# Revit family: expandable light position 2
name_source: partatom
category: Lighting Fixtures
units: mm (PartAtom-declared; Revit-internal decimal feet)

## family parameters
Always vertical = Yes
Cut with Voids When Loaded = No
Light Source = Yes
Maintain Annotation Orientation = No
OmniClass Number = 23.80.70.00
OmniClass Title = Lighting
Part Type = Normal
Room Calculation Point = No
Round Connector Dimension = Use Diameter
Shared = No
Work Plane-Based = No

## types (16) — shared parameters
Color Filter = 16777215
Default Elevation = 0' - 0"
Dimming Lamp Color Temperature Shift = <None>
MATERIAL CABLE = Steel, Paint Finish, Ivory, Glossy
MATERIAL LIGHT PIECE = Cloth, Lamp Shade
MATERIAL LIGHT PIECE ATTACHMENT = Steel, Paint Finish, Ivory, Glossy
MATERIAL ROOF ATTACHMENT PIECE = Steel, Paint Finish, Ivory, Glossy
Tilt Angle = 60.00°

## per-type parameters (varying)
| type | BOTTOM LIGHT PIECE HEIGHT | FLOOR TO ROOF HEIGHT | Photometric Web File | SUSPENDED CABLE LENGTH | TOP LIGHT PIECE HEIGHT |
| Totem Up-Down A-A | 1' - 2" | 9' - 0" | STELLA （D750MM）_IESNA2002.IES | 3' - 0" | 1' - 2" |
| Totem Up-Down A-B | 1' - 2" | 0' - 1 17/32" | generic | 2' - 0" | 0' - 10" |
| Totem Up-Down A-C | 1' - 2" | 0' - 1 17/32" | generic | 2' - 0" | 0' - 4 1/4" |
| Totem Up-Down A-D | 1' - 2" | 0' - 1 17/32" | generic | 2' - 0" | 0' - 3 13/32" |
| Totem Up-Down B-A | 0' - 10" | 0' - 1 17/32" | generic | 2' - 0" | 1' - 2" |
| Totem Up-Down B-B | 0' - 10" | 0' - 1 17/32" | generic | 2' - 0" | 0' - 10" |
| Totem Up-Down B-C | 0' - 10" | 0' - 1 17/32" | generic | 2' - 0" | 0' - 4 1/4" |
| Totem Up-Down B-D | 0' - 10" | 0' - 1 17/32" | generic | 2' - 0" | 0' - 3 13/32" |
| Totem Up-Down C-A | 0' - 4 1/4" | 0' - 1 17/32" | generic | 2' - 0" | 1' - 2" |
| Totem Up-Down C-B | 0' - 4 1/4" | 0' - 1 17/32" | generic | 2' - 0" | 0' - 10" |
| Totem Up-Down C-C | 0' - 4 1/4" | 0' - 1 17/32" | generic | 2' - 0" | 0' - 4 1/4" |
| Totem Up-Down C-D | 0' - 3 13/32" | 0' - 1 17/32" | generic | 2' - 0" | 0' - 4 1/4" |
| Totem Up-Down D-A | 0' - 3 13/32" | 0' - 1 17/32" | generic | 2' - 0" | 1' - 2" |
| Totem Up-Down D-B | 0' - 3 13/32" | 0' - 1 17/32" | generic | 2' - 0" | 0' - 10" |
| Totem Up-Down D-C | 0' - 3 13/32" | 0' - 1 17/32" | generic | 2' - 0" | 0' - 4 1/4" |
| Totem Up-Down D-D | 0' - 3 13/32" | 0' - 1 17/32" | generic | 2' - 0" | 0' - 3 13/32" |

## geometry (parser evidence)
native form markers: Sweep x3
no freeform markers — native parametric forms only
